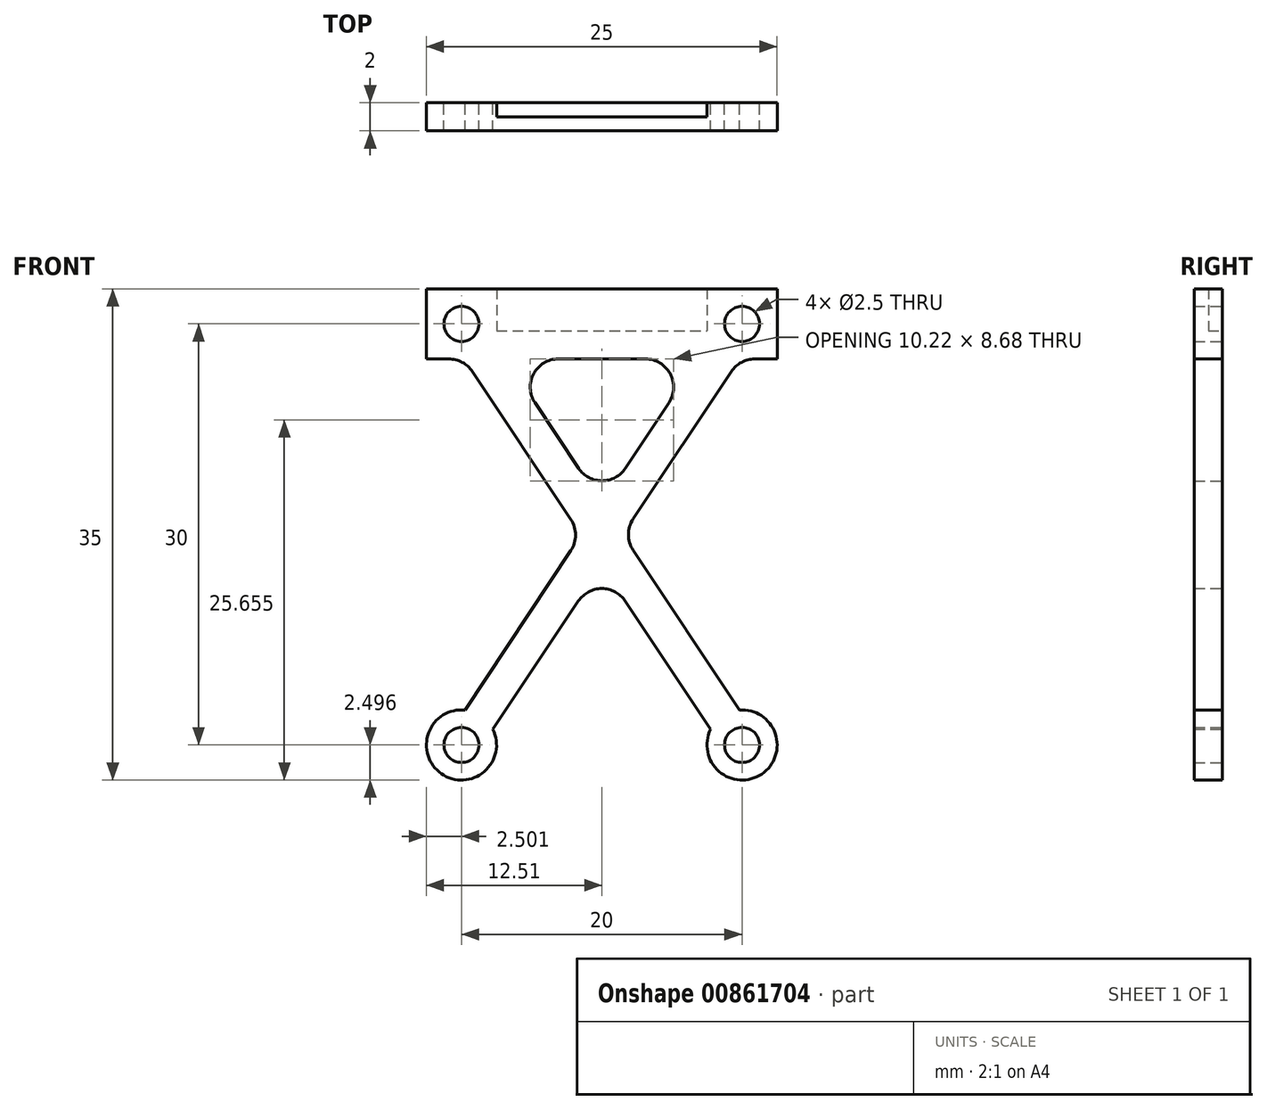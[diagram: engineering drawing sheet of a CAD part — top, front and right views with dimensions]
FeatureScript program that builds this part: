
annotation { "Feature Type Name" : "Feature", "Feature Type Description" : "" }
export const myFeature = defineFeature(function(context is Context, id is Id, definition is map)
    precondition{}
    {
        {
            var Q0;
            Q0=qCreatedBy(makeId("Front.planeOp"),FACE);
            var sketch = newSketch(context, id + "F0", { "sketchPlane" : qUnion([Q0])});
            skLineSegment(sketch, "E0.bottom", {"start": v(-6.75, 18.4) * mm, "end": v(8.25, 18.4) * mm});
            skLineSegment(sketch, "E0.top", {"start": v(-6.75, 15.4) * mm, "end": v(8.25, 15.4) * mm});
            skLineSegment(sketch, "E0.left", {"start": v(-6.75, 18.4) * mm, "end": v(-6.75, 15.4) * mm});
            skLineSegment(sketch, "E0.right", {"start": v(8.25, 18.4) * mm, "end": v(8.25, 15.4) * mm});
            skPoint(sketch, "E1.center.orphan", {"position": v(-6.75, 16.9) * mm});
            skPoint(sketch, "E2.center.orphan", {"position": v(8.25, 16.9) * mm});
            skSolve(sketch);
        }
        {
            var Q0;
            Q0=qCreatedBy(makeId("Front.planeOp"),FACE);
            var sketch = newSketch(context, id + "F1", { "sketchPlane" : qUnion([Q0])});
            skLineSegment(sketch, "E3.bottom", {"start": v(-11.75, 18.4) * mm, "end": v(13.25, 18.4) * mm});
            skLineSegment(sketch, "E3.top", {"start": v(-11.75, 13.4) * mm, "end": v(13.25, 13.4) * mm});
            skLineSegment(sketch, "E3.left", {"start": v(-11.75, 18.4) * mm, "end": v(-11.75, 13.4) * mm});
            skLineSegment(sketch, "E3.right", {"start": v(13.25, 18.4) * mm, "end": v(13.25, 13.4) * mm});
            skLineSegment(sketch, "E4.bottom", {"start": v(-8, 15.9) * mm, "end": v(9.5, 15.9) * mm, "construction": true});
            skLineSegment(sketch, "E4.top", {"start": v(-9.25, -14.1) * mm, "end": v(10.75, -14.1) * mm, "construction": true});
            skLineSegment(sketch, "E4.left", {"start": v(-9.25, 14.66) * mm, "end": v(-9.25, -14.1) * mm, "construction": true});
            skLineSegment(sketch, "E4.right", {"start": v(10.75, 14.66) * mm, "end": v(10.75, -14.1) * mm, "construction": true});
            skLineSegment(sketch, "E5", {"start": v(-23.14, 15.9) * mm, "end": v(-10.5, 15.9) * mm, "construction": true});
            skCircle(sketch, "E6", {"center": v(-9.25, 15.9) * mm, "radius": 1.25 * mm});
            skCircle(sketch, "E7", {"center": v(10.75, 15.9) * mm, "radius": 1.25 * mm});
            skLineSegment(sketch, "E8.trimOffspring", {"start": v(12, 15.9) * mm, "end": v(13.25, 15.9) * mm, "construction": true});
            skSolve(sketch);
        }
        {
            var Q0;
            Q0 = qSketchRegion(id + "F1", true);
            extrude(context, id + "F2", {"entities" : qUnion([Q0]), "depth" : 2 * mm, "offsetDistance" : 25 * mm});
        }
        {
            var Q0;
            Q0 = qSketchRegion(id + "F0", true);
            extrude(context, id + "F3", {"entities" : qUnion([Q0]), "operationType" : NewBodyOperationType.REMOVE, "depth" : 1 * mm, "offsetDistance" : 25 * mm});
        }
        {
            var Q0;
            Q0=qCreatedBy(makeId("Front.planeOp"),FACE);
            var sketch = newSketch(context, id + "F4", { "sketchPlane" : qUnion([Q0])});
            skLineSegment(sketch, "E9.bottom", {"start": v(-9.25, 15.9) * mm, "end": v(10.75, 15.9) * mm, "construction": true});
            skLineSegment(sketch, "E9.top", {"start": v(-9.25, -14.1) * mm, "end": v(10.75, -14.1) * mm, "construction": true});
            skLineSegment(sketch, "E9.left", {"start": v(-9.25, 15.9) * mm, "end": v(-9.25, -14.1) * mm, "construction": true});
            skLineSegment(sketch, "E9.right", {"start": v(10.75, 15.9) * mm, "end": v(10.75, -14.1) * mm, "construction": true});
            skLineSegment(sketch, "E10", {"start": v(-17.11, 15.9) * mm, "end": v(43.62, 15.9) * mm, "construction": true});
            skArc(sketch, "E11", {"start": v(9.7, 16.6) * mm, "mid": v(10.06, 14.87) * mm, "end": v(11.8, 15.21) * mm});
            skArc(sketch, "E12", {"start": v(-10.2, 15.1) * mm, "mid": v(-8.5, 14.9) * mm, "end": v(-8.2, 16.6) * mm});
            skCircle(sketch, "E13", {"center": v(10.75, -14.1) * mm, "radius": 1.25 * mm});
            skCircle(sketch, "E14", {"center": v(-9.25, -14.1) * mm, "radius": 1.25 * mm});
            skCircle(sketch, "E15", {"center": v(-9.25, -14.1) * mm, "radius": 2.5 * mm});
            skCircle(sketch, "E16", {"center": v(10.75, -14.1) * mm, "radius": 2.5 * mm});
            skLineSegment(sketch, "E17", {"start": v(-9.95, -13.06) * mm, "end": v(9.7, 16.6) * mm});
            skLineSegment(sketch, "E18", {"start": v(11.8, 15.21) * mm, "end": v(-8.2, -14.79) * mm});
            skLineSegment(sketch, "E19", {"start": v(11.62, -13.2) * mm, "end": v(-8.2, 16.6) * mm});
            skLineSegment(sketch, "E20", {"start": v(-10.2, 15.1) * mm, "end": v(9.71, -14.79) * mm});
            skSolve(sketch);
        }
        {
            var Q0;
            Q0 = qSketchRegion(id + "F4", true);
            extrude(context, id + "F5", {"entities" : qUnion([Q0]), "operationType" : NewBodyOperationType.ADD, "depth" : 2 * mm, "offsetDistance" : 25 * mm});
        }
        {
            var Q0;
            Q0=makeQuery(id+"F5.opExtrude","SWEPT_EDGE",EDGE,{"disambiguationData":[OSD([sQuery(id+"F4.wireOp",EDGE,"E17"),sQuery(id+"F4.wireOp",EDGE,"E19")])]});
            var Q1;
            Q1=makeQuery(id+"F5.opExtrude","SWEPT_EDGE",EDGE,{"disambiguationData":[OSD([sQuery(id+"F4.wireOp",EDGE,"E17"),sQuery(id+"F4.wireOp",EDGE,"E20")])]});
            var Q2;
            Q2=makeQuery(id+"F5.opExtrude","SWEPT_EDGE",EDGE,{"disambiguationData":[OSD([sQuery(id+"F4.wireOp",EDGE,"E18"),sQuery(id+"F4.wireOp",EDGE,"E19")])]});
            var Q3;
            Q3=makeQuery(id+"F5.opExtrude","SWEPT_EDGE",EDGE,{"disambiguationData":[OSD([sQuery(id+"F4.wireOp",EDGE,"E18"),sQuery(id+"F4.wireOp",EDGE,"E20")])]});
            var Q4;
            {var subQ0=sQuery(id+"F4.wireOp",EDGE,"E17");Q4=makeQuery(id+"F5.boolean.opBoolean","INTERSECT",EDGE,{"derivedFrom":[makeQuery(id+"F2.opExtrude","SWEPT_FACE",FACE,{"disambiguationData":[OSD([sQuery(id+"F1.wireOp",EDGE,"E3.top")])]}),makeQuery(id+"F5.opExtrude","SWEPT_FACE",FACE,{"disambiguationData":[OSD([subQ0]),TDD([makeQuery(id+"F4.imprint","IMPRINT",EDGE,{"disambiguationData":[TD([[makeQuery(id+"F4.imprint","INTERSECT",VERTEX,{"derivedFrom":[sQuery(id+"F4.wireOp",EDGE,"E11"),subQ0]}),1.0]])],"derivedFrom":subQ0})])]})]});}
            var Q5;
            {var subQ0=sQuery(id+"F4.wireOp",EDGE,"E19");Q5=makeQuery(id+"F5.boolean.opBoolean","INTERSECT",EDGE,{"derivedFrom":[makeQuery(id+"F2.opExtrude","SWEPT_FACE",FACE,{"disambiguationData":[OSD([sQuery(id+"F1.wireOp",EDGE,"E3.top")])]}),makeQuery(id+"F5.opExtrude","SWEPT_FACE",FACE,{"disambiguationData":[OSD([subQ0]),TDD([makeQuery(id+"F4.imprint","IMPRINT",EDGE,{"disambiguationData":[TD([[makeQuery(id+"F4.imprint","INTERSECT",VERTEX,{"derivedFrom":[sQuery(id+"F4.wireOp",EDGE,"E12"),subQ0]}),1.0]])],"derivedFrom":subQ0})])]})]});}
            var Q6;
            {var subQ0=sQuery(id+"F4.wireOp",EDGE,"E20");Q6=makeQuery(id+"F5.boolean.opBoolean","INTERSECT",EDGE,{"derivedFrom":[makeQuery(id+"F2.opExtrude","SWEPT_FACE",FACE,{"disambiguationData":[OSD([sQuery(id+"F1.wireOp",EDGE,"E3.top")])]}),makeQuery(id+"F5.opExtrude","SWEPT_FACE",FACE,{"disambiguationData":[OSD([subQ0]),TDD([makeQuery(id+"F4.imprint","IMPRINT",EDGE,{"disambiguationData":[TD([[makeQuery(id+"F4.imprint","INTERSECT",VERTEX,{"derivedFrom":[sQuery(id+"F4.wireOp",EDGE,"E12"),subQ0]}),-1.0]])],"derivedFrom":subQ0})])]})]});}
            var Q7;
            {var subQ0=sQuery(id+"F4.wireOp",EDGE,"E18");Q7=makeQuery(id+"F5.boolean.opBoolean","INTERSECT",EDGE,{"derivedFrom":[makeQuery(id+"F2.opExtrude","SWEPT_FACE",FACE,{"disambiguationData":[OSD([sQuery(id+"F1.wireOp",EDGE,"E3.top")])]}),makeQuery(id+"F5.opExtrude","SWEPT_FACE",FACE,{"disambiguationData":[OSD([subQ0]),TDD([makeQuery(id+"F4.imprint","IMPRINT",EDGE,{"disambiguationData":[TD([[makeQuery(id+"F4.imprint","INTERSECT",VERTEX,{"derivedFrom":[sQuery(id+"F4.wireOp",EDGE,"E11"),subQ0]}),-1.0]])],"derivedFrom":subQ0})])]})]});}
            fillet(context, id + "F6", {"entities" : qUnion([Q0, Q1, Q2, Q3, Q4, Q5, Q6, Q7]), "radius" : 2 * mm, "tangentPropagation" : true, "allowEdgeOverflow" : false});
        }
    });
